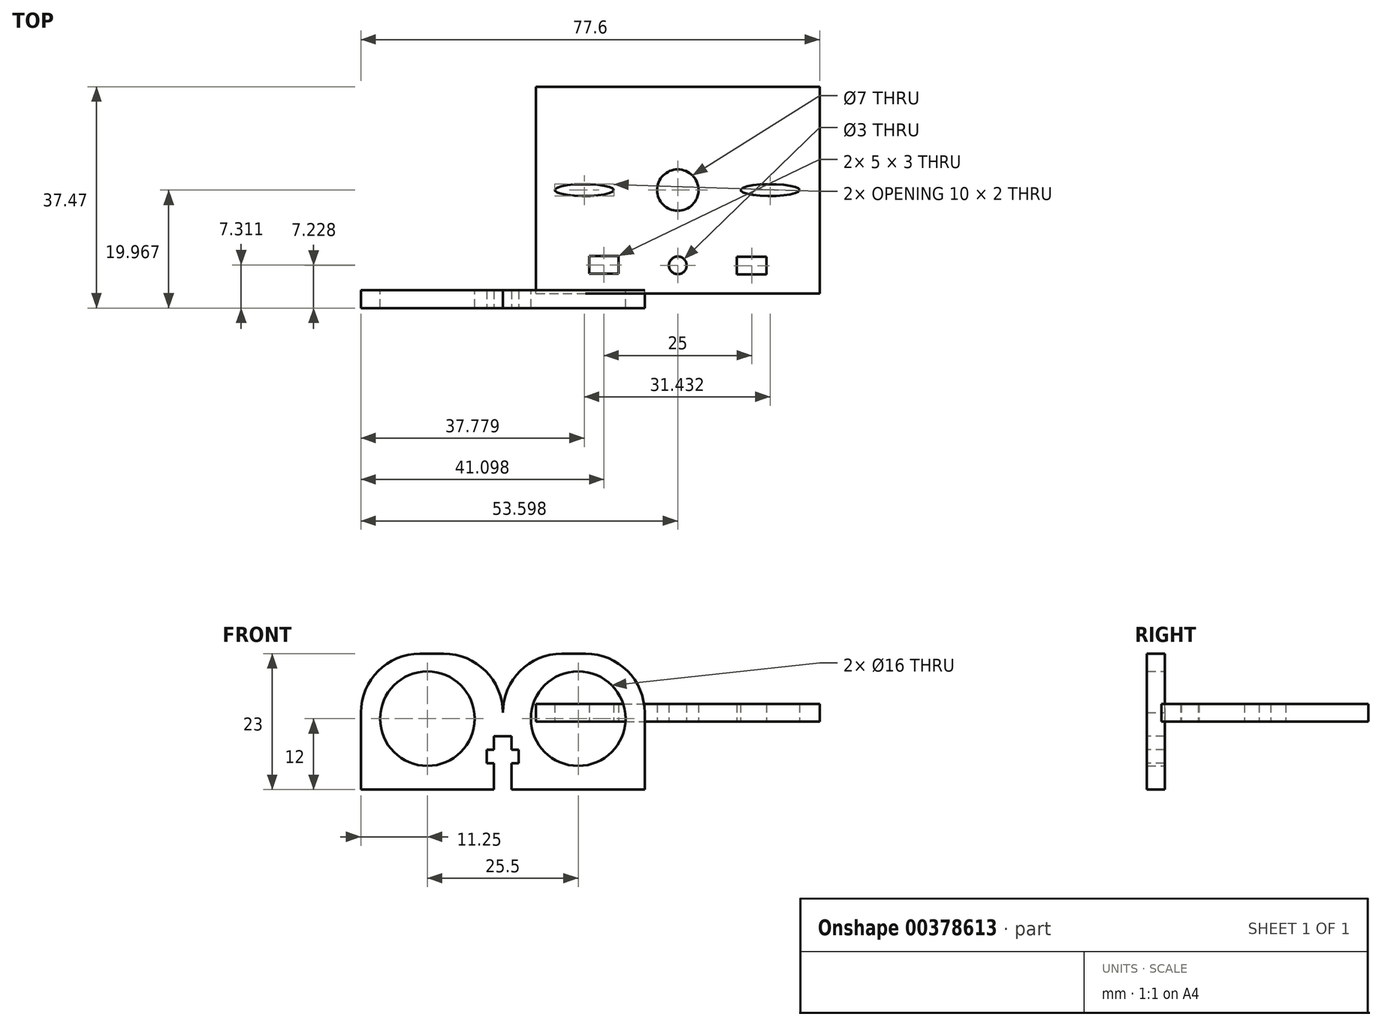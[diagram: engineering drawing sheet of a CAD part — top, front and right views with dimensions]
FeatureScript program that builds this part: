
annotation { "Feature Type Name" : "Feature", "Feature Type Description" : "" }
export const myFeature = defineFeature(function(context is Context, id is Id, definition is map)
    precondition{}
    {
        {
            var Q0;
            Q0=qCreatedBy(makeId("Front.planeOp"),FACE);
            var sketch = newSketch(context, id + "F0", { "sketchPlane" : qUnion([Q0])});
            skLineSegment(sketch, "E0.bottom", {"start": v(-14, 11.5) * mm, "end": v(-10, 11.5) * mm});
            skLineSegment(sketch, "E0.top", {"start": v(-24, -11.5) * mm, "end": v(24, -11.5) * mm});
            skLineSegment(sketch, "E0.left", {"start": v(-24, 1.5) * mm, "end": v(-24, -11.5) * mm});
            skLineSegment(sketch, "E0.right", {"start": v(24, 1.5) * mm, "end": v(24, -11.5) * mm});
            skCircle(sketch, "E1", {"center": v(12.75, 0.5) * mm, "radius": 8 * mm});
            skLineSegment(sketch, "E2", {"start": v(-25.8, 0.5) * mm, "end": v(24, 0.5) * mm, "construction": true});
            skCircle(sketch, "E3", {"center": v(-12.75, 0.5) * mm, "radius": 8 * mm});
            skLineSegment(sketch, "E4", {"start": v(0, 0) * mm, "end": v(0, 15.43) * mm, "construction": true});
            skLineSegment(sketch, "E5", {"start": v(0, 1.5) * mm, "end": v(0, -15.07) * mm, "construction": true});
            skLineSegment(sketch, "E6.bottom", {"start": v(-15, -11.5) * mm, "end": v(-10, -11.5) * mm});
            skLineSegment(sketch, "E6.top", {"start": v(-15, -14.5) * mm, "end": v(-10, -14.5) * mm});
            skLineSegment(sketch, "E6.left", {"start": v(-15, -11.5) * mm, "end": v(-15, -14.5) * mm});
            skLineSegment(sketch, "E6.right", {"start": v(-10, -11.5) * mm, "end": v(-10, -14.5) * mm});
            skLineSegment(sketch, "E7.bottom", {"start": v(10, -11.5) * mm, "end": v(15, -11.5) * mm});
            skLineSegment(sketch, "E7.top", {"start": v(10, -14.5) * mm, "end": v(15, -14.5) * mm});
            skLineSegment(sketch, "E7.left", {"start": v(10, -11.5) * mm, "end": v(10, -14.5) * mm});
            skLineSegment(sketch, "E7.right", {"start": v(15, -11.5) * mm, "end": v(15, -14.5) * mm});
            skPoint(sketch, "E8.visualSharp", {"position": v(-24, 11.5) * mm});
            skArc(sketch, "E8.filletArc", {"start": v(-14, 11.5) * mm, "mid": v(-21.07, 8.57) * mm, "end": v(-24, 1.5) * mm});
            skPoint(sketch, "E9.visualSharp", {"position": v(24, 11.5) * mm});
            skArc(sketch, "E9.filletArc", {"start": v(24, 1.5) * mm, "mid": v(21.07, 8.57) * mm, "end": v(14, 11.5) * mm});
            skArc(sketch, "E10.filletArc", {"start": v(0, 1.5) * mm, "mid": v(-2.93, 8.57) * mm, "end": v(-10, 11.5) * mm});
            skArc(sketch, "E11.MirrorCS", {"start": v(0, 1.5) * mm, "mid": v(2.93, 8.57) * mm, "end": v(10, 11.5) * mm});
            skLineSegment(sketch, "E12", {"start": v(10, 11.5) * mm, "end": v(14, 11.5) * mm});
            skSolve(sketch);
        }
        {
            var Q0;
            Q0=qCreatedBy(makeId("Top.planeOp"),FACE);
            var sketch = newSketch(context, id + "F1", { "sketchPlane" : qUnion([Q0])});
            skLineSegment(sketch, "E13.bottom", {"start": v(5.6, -0.53) * mm, "end": v(53.6, -0.53) * mm});
            skLineSegment(sketch, "E13.top", {"start": v(5.6, 34.47) * mm, "end": v(53.6, 34.47) * mm});
            skLineSegment(sketch, "E13.left", {"start": v(5.6, -0.53) * mm, "end": v(5.6, 34.47) * mm});
            skLineSegment(sketch, "E13.right", {"start": v(53.6, -0.53) * mm, "end": v(53.6, 34.47) * mm});
            skLineSegment(sketch, "E14", {"start": v(5.6, 16.97) * mm, "end": v(53.6, 16.97) * mm, "construction": true});
            skEllipse(sketch, "E15", {"center": v(13.78, 16.97) * mm, "majorRadius": 5 * mm, "minorRadius": 1 * mm, "majorAxis": v(1, 0)});
            skEllipse(sketch, "E16", {"center": v(45.21, 16.97) * mm, "majorRadius": 5 * mm, "minorRadius": 1 * mm, "majorAxis": v(1, 0)});
            skLineSegment(sketch, "E17", {"start": v(29.6, 34.47) * mm, "end": v(29.6, 0) * mm, "construction": true});
            skCircle(sketch, "E18", {"center": v(29.6, 16.97) * mm, "radius": 3.5 * mm});
            skLineSegment(sketch, "E19.bottom", {"start": v(14.6, 5.81) * mm, "end": v(19.6, 5.81) * mm});
            skLineSegment(sketch, "E19.top", {"start": v(14.6, 2.81) * mm, "end": v(19.6, 2.81) * mm});
            skLineSegment(sketch, "E19.left", {"start": v(14.6, 5.81) * mm, "end": v(14.6, 2.81) * mm});
            skLineSegment(sketch, "E19.right", {"start": v(19.6, 5.81) * mm, "end": v(19.6, 2.81) * mm});
            skLineSegment(sketch, "E20.bottom", {"start": v(39.6, 5.68) * mm, "end": v(44.6, 5.68) * mm});
            skLineSegment(sketch, "E20.top", {"start": v(39.6, 2.68) * mm, "end": v(44.6, 2.68) * mm});
            skLineSegment(sketch, "E20.left", {"start": v(39.6, 5.68) * mm, "end": v(39.6, 2.68) * mm});
            skLineSegment(sketch, "E20.right", {"start": v(44.6, 5.68) * mm, "end": v(44.6, 2.68) * mm});
            skLineSegment(sketch, "E21", {"start": v(5.6, 4.14) * mm, "end": v(53.6, 4.31) * mm, "construction": true});
            skPoint(sketch, "E21.endSnap0", {"position": v(19.6, 4.31) * mm});
            skCircle(sketch, "E22", {"center": v(29.6, 4.23) * mm, "radius": 1.5 * mm});
            skSolve(sketch);
        }
        {
            var Q0;
            Q0=qSketchRegion(id+"F1",true);
            extrude(context, id + "F2", {"entities" : qUnion([Q0]), "depth" : 3 * mm});
        }
        {
            var Q0;
            Q0=makeQuery(id+"F0.imprint","IMPRINT",FACE,{"disambiguationData":[TD([[makeQuery(id+"F0.imprint","IMPRINT",EDGE,{"derivedFrom":sQuery(id+"F0.wireOp",EDGE,"E0.bottom")}),-1.0]])]});
            var Q1;
            Q1=makeQuery(id+"F0.imprint","IMPRINT",FACE,{"disambiguationData":[TD([[makeQuery(id+"F0.imprint","IMPRINT",EDGE,{"derivedFrom":sQuery(id+"F0.wireOp",EDGE,"E6.bottom")}),-1.0]])]});
            var Q2;
            Q2=makeQuery(id+"F0.imprint","IMPRINT",FACE,{"disambiguationData":[TD([[makeQuery(id+"F0.imprint","IMPRINT",EDGE,{"derivedFrom":sQuery(id+"F0.wireOp",EDGE,"E7.bottom")}),-1.0]])]});
            extrude(context, id + "F3", {"entities" : qUnion([Q0, Q1, Q2]), "depth" : 3 * mm});
        }
        {
            var Q0;
            Q0=makeQuery(id+"F3.opExtrude","CAP_FACE",FACE,{"disambiguationData":[OSD([sQuery(id+"F0.wireOp",EDGE,"E0.bottom"),sQuery(id+"F0.wireOp",EDGE,"E0.top"),sQuery(id+"F0.wireOp",EDGE,"E0.left"),sQuery(id+"F0.wireOp",EDGE,"E0.right"),sQuery(id+"F0.wireOp",EDGE,"E1"),sQuery(id+"F0.wireOp",EDGE,"E3"),sQuery(id+"F0.wireOp",EDGE,"E6.top"),sQuery(id+"F0.wireOp",EDGE,"E6.left"),sQuery(id+"F0.wireOp",EDGE,"E6.right"),sQuery(id+"F0.wireOp",EDGE,"E7.top"),sQuery(id+"F0.wireOp",EDGE,"E7.left"),sQuery(id+"F0.wireOp",EDGE,"E7.right")])],"isStart":false});
            var sketch = newSketch(context, id + "F4", { "sketchPlane" : qUnion([Q0])});
            skLineSegment(sketch, "E23.bottom", {"start": v(-1.5, -2.5) * mm, "end": v(1.5, -2.5) * mm});
            skLineSegment(sketch, "E23.top", {"start": v(-1.5, -11.5) * mm, "end": v(1.5, -11.5) * mm});
            skLineSegment(sketch, "E23.left", {"start": v(-1.5, -2.5) * mm, "end": v(-1.5, -11.5) * mm});
            skLineSegment(sketch, "E23.right", {"start": v(1.5, -2.5) * mm, "end": v(1.5, -11.5) * mm});
            skLineSegment(sketch, "E24.bottom", {"start": v(-2.7, -4.75) * mm, "end": v(2.7, -4.75) * mm});
            skLineSegment(sketch, "E24.top", {"start": v(-2.7, -7.05) * mm, "end": v(2.7, -7.05) * mm});
            skLineSegment(sketch, "E24.left", {"start": v(-2.7, -4.75) * mm, "end": v(-2.7, -7.05) * mm});
            skLineSegment(sketch, "E24.right", {"start": v(2.7, -4.75) * mm, "end": v(2.7, -7.05) * mm});
            skSolve(sketch);
        }
        {
            var Q0;
            {var subQ0=sQuery(id+"F4.wireOp",EDGE,"E23.top");Q0=makeQuery(id+"F4.imprint","IMPRINT",FACE,{"disambiguationData":[TD([[makeQuery(id+"F4.imprint","IMPRINT",EDGE,{"derivedFrom":subQ0}),1.0]])]});}
            var Q1;
            {var subQ0=sQuery(id+"F4.wireOp",EDGE,"E24.bottom");var subQ1=sQuery(id+"F4.wireOp",EDGE,"E23.left");var subQ2=makeQuery(id+"F4.imprint","INTERSECT",VERTEX,{"derivedFrom":[subQ1,subQ0]});Q1=makeQuery(id+"F4.imprint","IMPRINT",FACE,{"disambiguationData":[TD([[makeQuery(id+"F4.imprint","IMPRINT",EDGE,{"disambiguationData":[TD([[subQ2,-1.0]])],"derivedFrom":subQ1}),1.0]])]});}
            var Q2;
            {var subQ5=sQuery(id+"F4.wireOp",EDGE,"E24.left");Q2=makeQuery(id+"F4.imprint","IMPRINT",FACE,{"disambiguationData":[TD([[makeQuery(id+"F4.imprint","IMPRINT",EDGE,{"derivedFrom":subQ5}),1.0]])]});}
            var Q3;
            {var subQ0=sQuery(id+"F4.wireOp",EDGE,"E23.bottom");Q3=makeQuery(id+"F4.imprint","IMPRINT",FACE,{"disambiguationData":[TD([[makeQuery(id+"F4.imprint","IMPRINT",EDGE,{"derivedFrom":subQ0}),-1.0]])]});}
            var Q4;
            {var subQ5=sQuery(id+"F4.wireOp",EDGE,"E24.right");Q4=makeQuery(id+"F4.imprint","IMPRINT",FACE,{"disambiguationData":[TD([[makeQuery(id+"F4.imprint","IMPRINT",EDGE,{"derivedFrom":subQ5}),-1.0]])]});}
            extrude(context, id + "F5", {"entities" : qUnion([Q0, Q1, Q2, Q3, Q4]), "operationType" : NewBodyOperationType.REMOVE, "oppositeDirection" : true, "depth" : 25 * mm});
        }
    });
